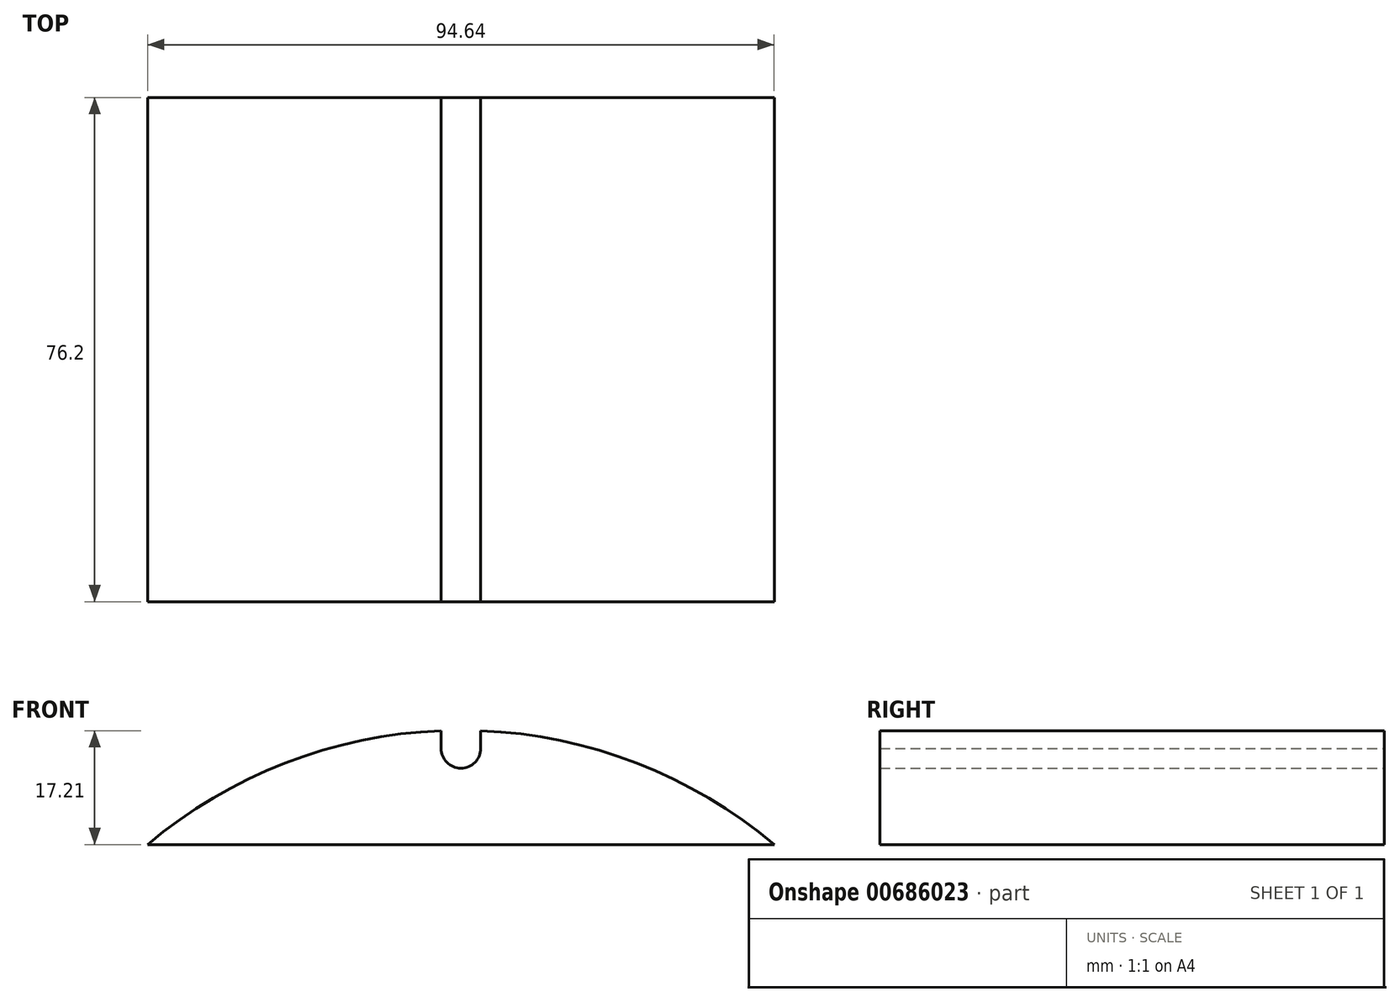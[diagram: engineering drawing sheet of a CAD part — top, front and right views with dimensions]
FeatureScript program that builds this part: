
annotation { "Feature Type Name" : "Feature", "Feature Type Description" : "" }
export const myFeature = defineFeature(function(context is Context, id is Id, definition is map)
    precondition{}
    {
        {
            var Q0;
            Q0=qCreatedBy(makeId("Front.planeOp"),FACE);
            var sketch = newSketch(context, id + "F0", { "sketchPlane" : qUnion([Q0])});
            skCircle(sketch, "E0", {"center": v(0, 0) * mm, "radius": 73.47 * mm});
            skLineSegment(sketch, "E1.bottom", {"start": v(-75.18, 56.2) * mm, "end": v(75.18, 56.2) * mm});
            skLineSegment(sketch, "E1.top", {"start": v(-75.18, -64.76) * mm, "end": v(75.18, -64.76) * mm});
            skLineSegment(sketch, "E1.left", {"start": v(-75.18, 56.2) * mm, "end": v(-75.18, -64.76) * mm});
            skLineSegment(sketch, "E1.right", {"start": v(75.18, 56.2) * mm, "end": v(75.18, -64.76) * mm});
            skCircle(sketch, "E2", {"center": v(0, 70.72) * mm, "radius": 3 * mm});
            skLineSegment(sketch, "E3.bottom", {"start": v(3, 70.72) * mm, "end": v(-3.02, 70.72) * mm});
            skLineSegment(sketch, "E3.top", {"start": v(3, 75.98) * mm, "end": v(-3.02, 75.98) * mm});
            skLineSegment(sketch, "E3.left", {"start": v(3, 70.72) * mm, "end": v(3, 75.98) * mm});
            skLineSegment(sketch, "E3.right", {"start": v(-3.02, 70.72) * mm, "end": v(-3.02, 75.98) * mm});
            skLineSegment(sketch, "E4.bottom", {"start": v(-50.8, 46.04) * mm, "end": v(50.8, 46.04) * mm});
            skLineSegment(sketch, "E4.top", {"start": v(-50.8, 39.69) * mm, "end": v(50.8, 39.69) * mm});
            skLineSegment(sketch, "E4.left", {"start": v(-50.8, 46.04) * mm, "end": v(-50.8, 39.69) * mm});
            skLineSegment(sketch, "E4.right", {"start": v(50.8, 46.04) * mm, "end": v(50.8, 39.69) * mm});
            skSolve(sketch);
        }
        {
            var Q0;
            {var subQ0=sQuery(id+"F0.wireOp",EDGE,"E3.left");var subQ6=sQuery(id+"F0.wireOp",EDGE,"E0");var subQ11=makeQuery(id+"F0.imprint","INTERSECT",VERTEX,{"derivedFrom":[subQ6,subQ0]});Q0=makeQuery(id+"F0.imprint","IMPRINT",FACE,{"disambiguationData":[TD([[makeQuery(id+"F0.imprint","IMPRINT",EDGE,{"disambiguationData":[TD([[subQ11,1.0]])],"derivedFrom":subQ6}),1.0]])]});}
            extrude(context, id + "F1", {"entities" : qUnion([Q0]), "depth" : 76.2 * mm, "offsetDistance" : 25.4 * mm});
        }
    });
